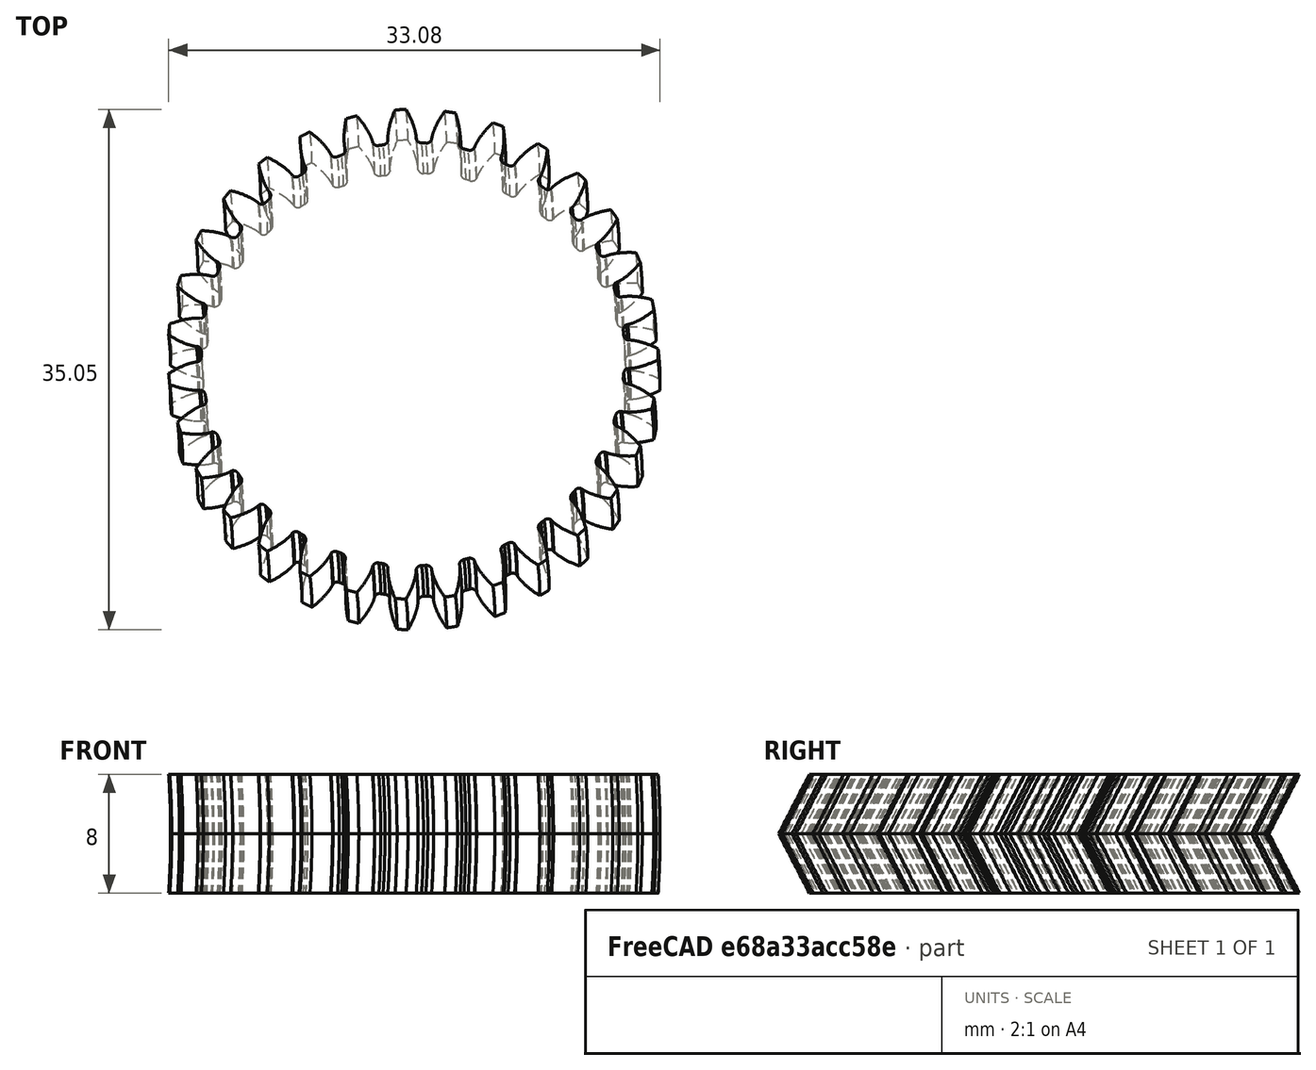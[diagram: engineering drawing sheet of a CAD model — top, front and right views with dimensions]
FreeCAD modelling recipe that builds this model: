
FCSTD DOCUMENT  (FreeCAD 0.17R13541 (Git))
Label: Gear6
License: All rights reserved
LicenseURL: http://en.wikipedia.org/wiki/All_rights_reserved
objects: Part::Helix×2, PartDesign::ShapeBinder×2, PartDesign::AdditivePipe×2, Part::Part2DObjectPython×1, PartDesign::Body×1
note: 10 computed .brp shape members not serialized (recipe doc carries the construction recipe); baked Part::Feature solids carry a one-line shape summary decoded from their .brp

FEATURE [Part::Part2DObjectPython] InvoluteGear  # Draft 2D object (typed FeaturePython)
  ExternalGear = true
  HighPrecision = true
  Modules = 1
  NumberOfTeeth = 31
  PressureAngle = 20
FEATURE [Part::Helix] Helix
  Angle = 0
  AttacherType = Attacher::AttachEngine3D
  Height = 4
  LocalCoord = 0
  Pitch = 200
  Radius = 16.5
  Style = 1
FEATURE [PartDesign::ShapeBinder] ReferenceHelix
  Support = -> [Helix]
FEATURE [Part::Helix] Helix001
  Angle = 0
  AttacherType = Attacher::AttachEngine3D
  Height = 4
  LocalCoord = 1
  Pitch = 200
  Placement = pos=(0,0,0) rot=(1,0,0;3.14159rad)
  Radius = 16.5
  Style = 1
FEATURE [PartDesign::AdditivePipe] AdditivePipe
  AuxilleryCurvelinear = true
  AuxillerySpineTangent = false
  Binormal = (0,0,0)
  Mode = 1
  Profile = -> InvoluteGear
  Spine = -> ReferenceHelix
  SpineTangent = false
  Transformation = 0
  Transition = 1
FEATURE [PartDesign::ShapeBinder] CopyHelix001
  Placement = pos=(0,0,0) rot=(1,0,0;3.14159rad)
FEATURE [PartDesign::AdditivePipe] AdditivePipe001
  AuxilleryCurvelinear = true
  AuxillerySpineTangent = false
  BaseFeature = -> AdditivePipe
  Binormal = (0,0,0)
  Mode = 1
  Profile = -> InvoluteGear
  Spine = -> CopyHelix001
  SpineTangent = false
  Transformation = 0
  Transition = 0
FEATURE [PartDesign::Body] Body
  Group = -> [InvoluteGear,ReferenceHelix,AdditivePipe,AdditivePipe001,CopyHelix001]
  Origin = -> Origin
  Tip = -> AdditivePipe001
